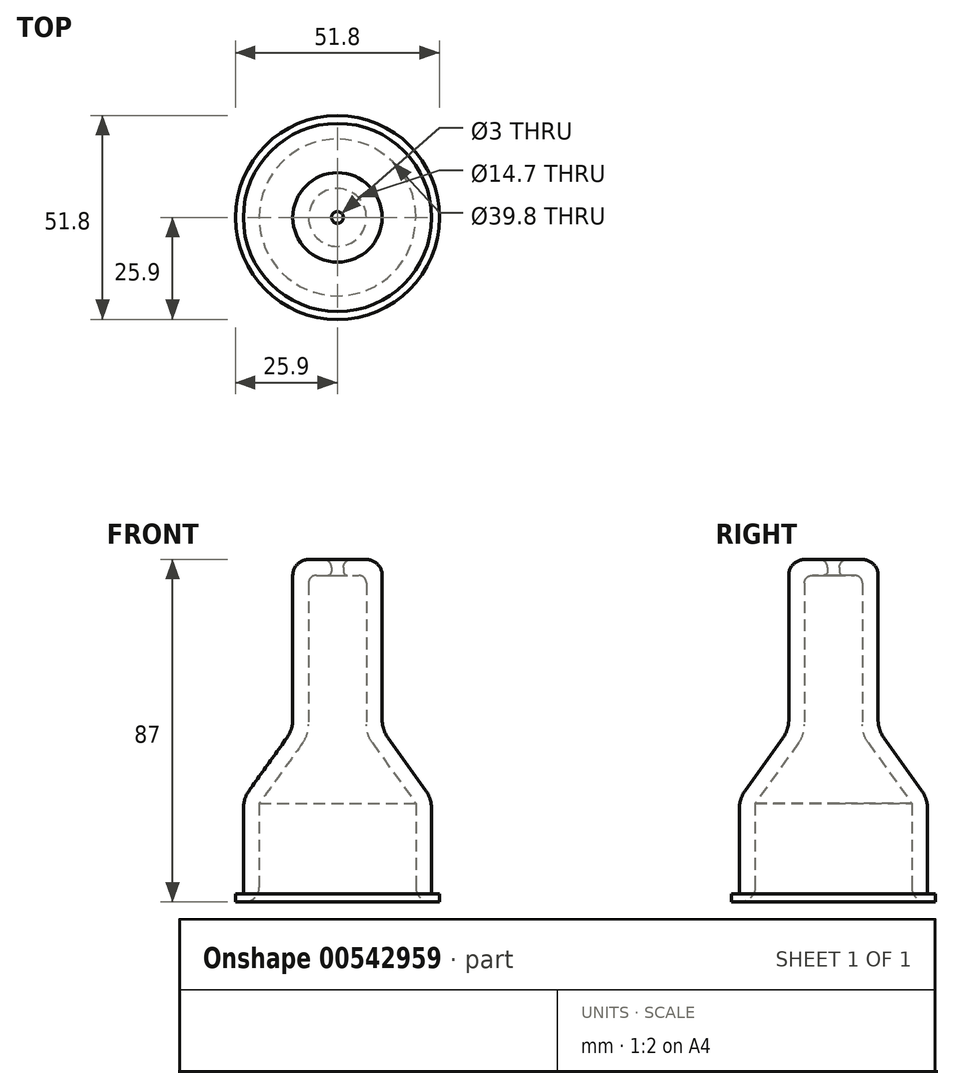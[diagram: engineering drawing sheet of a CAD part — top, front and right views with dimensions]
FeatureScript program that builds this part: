
annotation { "Feature Type Name" : "Feature", "Feature Type Description" : "" }
export const myFeature = defineFeature(function(context is Context, id is Id, definition is map)
    precondition{}
    {
        {
            var Q0;
            Q0=qCreatedBy(makeId("Front.planeOp"),FACE);
            var sketch = newSketch(context, id + "F0", { "sketchPlane" : qUnion([Q0])});
            skLineSegment(sketch, "E0", {"start": v(19.9, 3.75) * mm, "end": v(19.9, 25) * mm});
            skLineSegment(sketch, "E1", {"start": v(19.9, 25) * mm, "end": v(8.85, 40.4) * mm});
            skLineSegment(sketch, "E2", {"start": v(7.35, 45.07) * mm, "end": v(7.35, 81) * mm});
            skLineSegment(sketch, "E3", {"start": v(5.35, 83) * mm, "end": v(2.5, 83) * mm});
            skLineSegment(sketch, "E4", {"start": v(3.5, 87) * mm, "end": v(7.35, 87) * mm});
            skLineSegment(sketch, "E5", {"start": v(11.35, 83) * mm, "end": v(11.35, 46.36) * mm});
            skLineSegment(sketch, "E6", {"start": v(12.85, 41.7) * mm, "end": v(22.4, 28.38) * mm});
            skLineSegment(sketch, "E7", {"start": v(23.9, 0) * mm, "end": v(23.65, 0) * mm});
            skPoint(sketch, "E8.visualSharp", {"position": v(7.35, 42.5) * mm});
            skArc(sketch, "E8.filletArc", {"start": v(7.35, 45.07) * mm, "mid": v(7.73, 42.62) * mm, "end": v(8.85, 40.4) * mm});
            skPoint(sketch, "E9.visualSharp", {"position": v(11.35, 87) * mm});
            skArc(sketch, "E9.filletArc", {"start": v(11.35, 83) * mm, "mid": v(10.18, 85.83) * mm, "end": v(7.35, 87) * mm});
            skArc(sketch, "E10.filletArc", {"start": v(23.9, 23.71) * mm, "mid": v(23.52, 26.16) * mm, "end": v(22.4, 28.38) * mm});
            skLineSegment(sketch, "E11", {"start": v(1.5, 84) * mm, "end": v(1.5, 85) * mm});
            skLineSegment(sketch, "E12", {"start": v(23.9, 0) * mm, "end": v(25.9, 0) * mm});
            skLineSegment(sketch, "E13", {"start": v(25.9, 0) * mm, "end": v(25.9, 2) * mm});
            skLineSegment(sketch, "E14", {"start": v(25.9, 2) * mm, "end": v(24.4, 2) * mm});
            skLineSegment(sketch, "E15", {"start": v(23.9, 23.71) * mm, "end": v(23.9, 2.5) * mm});
            skPoint(sketch, "E16.visualSharp", {"position": v(11.35, 43.79) * mm});
            skArc(sketch, "E16.filletArc", {"start": v(11.35, 46.36) * mm, "mid": v(11.73, 43.9) * mm, "end": v(12.85, 41.7) * mm});
            skPoint(sketch, "E17.visualSharp", {"position": v(23.9, 2) * mm});
            skArc(sketch, "E17.filletArc", {"start": v(23.9, 2.5) * mm, "mid": v(24.05, 2.15) * mm, "end": v(24.4, 2) * mm});
            skPoint(sketch, "E18.visualSharp", {"position": v(1.5, 87) * mm});
            skArc(sketch, "E18.filletArc", {"start": v(3.5, 87) * mm, "mid": v(2.09, 86.41) * mm, "end": v(1.5, 85) * mm});
            skPoint(sketch, "E19.visualSharp", {"position": v(1.5, 83) * mm});
            skArc(sketch, "E19.filletArc", {"start": v(1.5, 84) * mm, "mid": v(1.8, 83.3) * mm, "end": v(2.5, 83) * mm});
            skPoint(sketch, "E20.visualSharp", {"position": v(19.9, 0) * mm});
            skArc(sketch, "E20.filletArc", {"start": v(19.9, 3.75) * mm, "mid": v(21, 1.1) * mm, "end": v(23.65, 0) * mm});
            skArc(sketch, "E21.filletArc", {"start": v(7.35, 81) * mm, "mid": v(6.76, 82.41) * mm, "end": v(5.35, 83) * mm});
            skSolve(sketch);
        }
        {
            var Q0;
            Q0=qCreatedBy(makeId("Front.planeOp"),FACE);
            var sketch = newSketch(context, id + "F1", { "sketchPlane" : qUnion([Q0])});
            skLineSegment(sketch, "E22", {"start": v(0, 0) * mm, "end": v(0, 26.94) * mm, "construction": true});
            skSolve(sketch);
        }
        {
            var Q0;
            Q0=makeQuery(id+"F0.imprint","IMPRINT",FACE,{"disambiguationData":[TD([[makeQuery(id+"F0.imprint","IMPRINT",EDGE,{"derivedFrom":sQuery(id+"F0.wireOp",EDGE,"E0")}),-1.0]])]});
            var Q1;
            Q1=sQuery(id+"F1.wireOp",EDGE,"E22");
            revolve(context, id + "F2", {"entities" : qUnion([Q0]), "axis" : qUnion([Q1]), "revolveType" : RevolveType.FULL});
        }
    });
